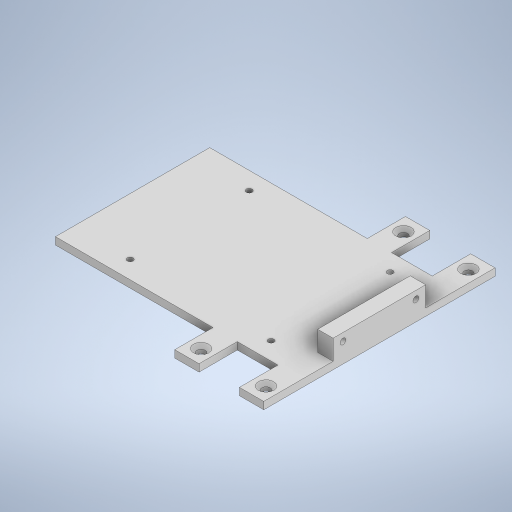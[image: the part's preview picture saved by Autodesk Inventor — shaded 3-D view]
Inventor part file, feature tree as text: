
AUTODESK INVENTOR PART (.ipt)
format: ipt  version: 2024.1 (Build 281209000, 209)  size: 311,296 bytes
history: native  units: in
note: dims shown in document units (in); Inventor stores cm internally (conversion verified against a paired STEP export)
features: sketch x5, hole x3, extrude x2
ambient origin geometry x8: Origin, YZ Plane, XZ Plane, XY Plane, X Axis, Y Axis, Z Axis, Center Point
bodies: Solid1 (feature_tree)
feature tree (10):
  extrude  "Extrusion1"  Depth=3.7402in
  hole  "Hole1"  [1 undecoded]
  extrude  "Extrusion2"  Depth=2.5in
  hole  "Hole2"  [1 undecoded]
  hole  "Hole3"  [1 undecoded]
  sketch  "Sketch1"  dims[d0=0.3937in d1=3.7402in]
  sketch  "Sketch2"  dims[d2=0.1181in d3=0.0in d4=1.6398in]
  sketch  "Sketch3"  dims[d5=1.6398in]
  sketch  "Sketch4"  dims[d6=0.134in d7=0.75in d8=0.248in d9=0.25in d10=90.0deg d11=1.0in d12=0.8108in d13=2.5in]
  sketch  "Sketch5"  dims[d14=2.5in d15=1.5in d16=0.125in d17=1.5in d18=0.325in d19=0.0in d20=0.125in d21=0.5906in d22=1.1811in d23=0.094in d24=0.75in d25=0.173in d26=0.141in d27=90.0deg d28=1.0in d29=0.8108in d30=0.9646in d31=1.9291in d32=3.3465in d33=0.1378in d34=0.1378in d35=0.1378in d36=0.1378in d37=2.2835in d38=180.0deg d39=2.2835in d40=0.094in d41=0.75in d42=0.375in d43=0.25in d44=0.5635in d45=1.0in d46=0.8108in d47=0.197in d48=3.749in d49=1.64in d50=1.64in]
note: 3 required parameter values undecoded (feature->parameter linkage not recoverable at this tier; creation-order binding heuristic only, values carry confidence <= 0.55)
